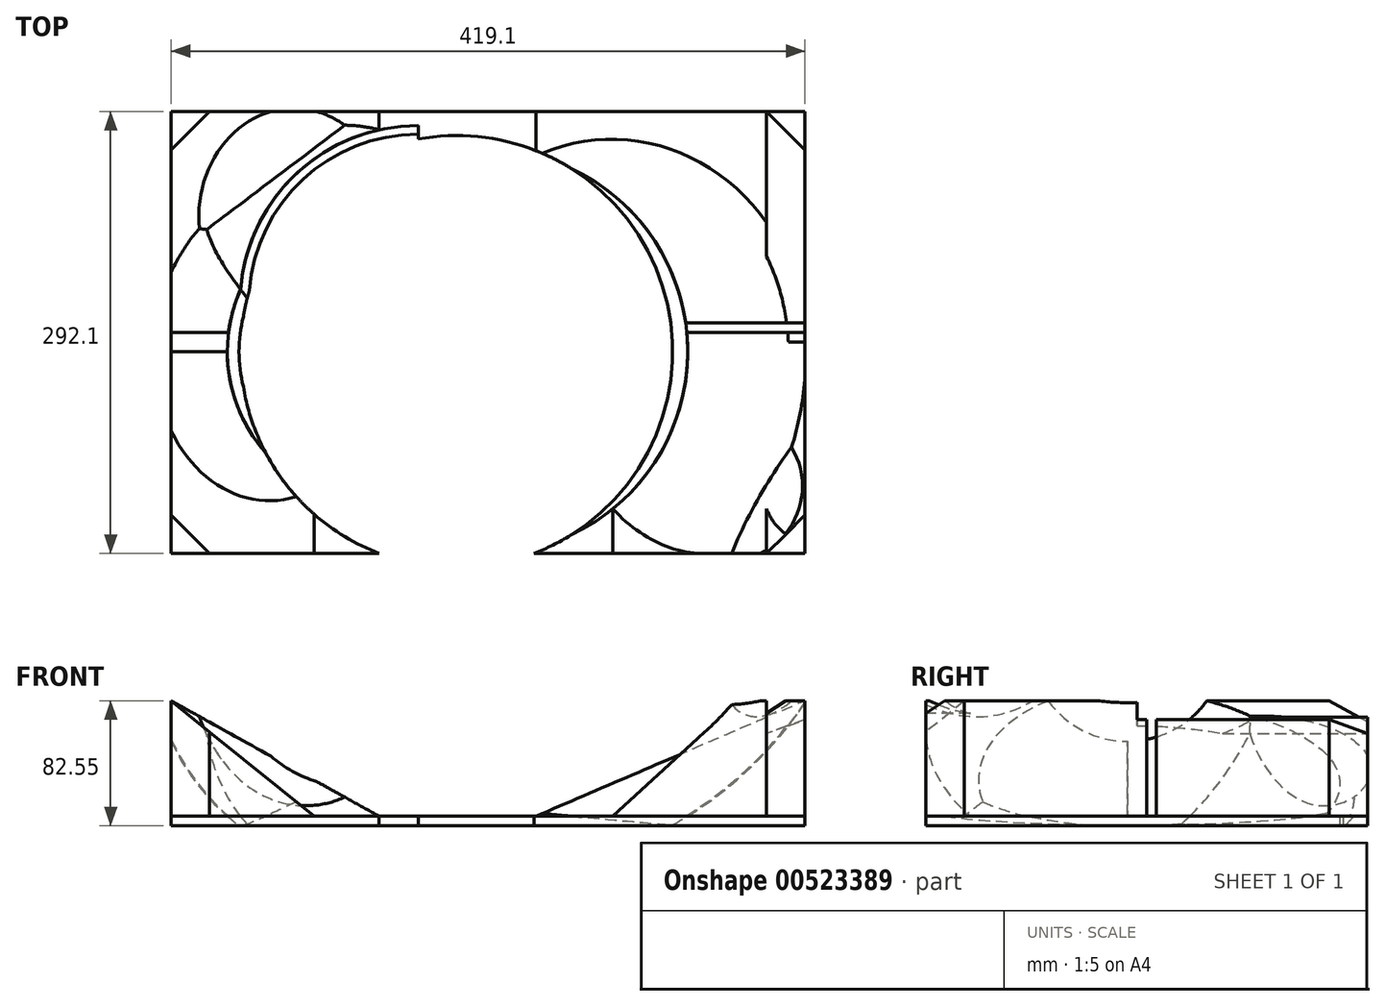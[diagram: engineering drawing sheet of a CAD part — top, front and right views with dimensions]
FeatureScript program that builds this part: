
annotation { "Feature Type Name" : "Feature", "Feature Type Description" : "" }
export const myFeature = defineFeature(function(context is Context, id is Id, definition is map)
    precondition{}
    {
        {
            var Q0;
            Q0=qCreatedBy(makeId("Top.planeOp"),FACE);
            var sketch = newSketch(context, id + "F0", { "sketchPlane" : qUnion([Q0])});
            skLineSegment(sketch, "E0.bottom", {"start": v(-188.72, 158.75) * mm, "end": v(230.38, 158.75) * mm});
            skLineSegment(sketch, "E0.top", {"start": v(-188.72, -133.35) * mm, "end": v(230.38, -133.35) * mm});
            skLineSegment(sketch, "E0.left", {"start": v(-188.72, 158.75) * mm, "end": v(-188.72, -133.35) * mm});
            skLineSegment(sketch, "E0.right", {"start": v(230.38, 158.75) * mm, "end": v(230.38, -133.35) * mm});
            skCircle(sketch, "E1", {"center": v(0, 0) * mm, "radius": 142.88 * mm});
            skSolve(sketch);
        }
        {
            var Q0;
            Q0=makeQuery(id+"F0.imprint","IMPRINT",FACE,{"disambiguationData":[TD([[makeQuery(id+"F0.imprint","IMPRINT",EDGE,{"derivedFrom":sQuery(id+"F0.wireOp",EDGE,"E0.bottom")}),-1.0]])]});
            extrude(context, id + "F1", {"entities" : qUnion([Q0]), "oppositeDirection" : true, "depth" : 6.35 * mm, "offsetDistance" : 25.4 * mm});
        }
        {
            var Q0;
            Q0=makeQuery(id+"F1.opExtrude","CAP_FACE",FACE,{"disambiguationData":[OSD([sQuery(id+"F0.wireOp",EDGE,"E0.bottom"),sQuery(id+"F0.wireOp",EDGE,"E0.top"),sQuery(id+"F0.wireOp",EDGE,"E0.left"),sQuery(id+"F0.wireOp",EDGE,"E0.right"),sQuery(id+"F0.wireOp",EDGE,"E1")])],"isStart":true});
            var sketch = newSketch(context, id + "F2", { "sketchPlane" : qUnion([Q0])});
            skLineSegment(sketch, "E2.bottom", {"start": v(230.38, 158.75) * mm, "end": v(52.58, 158.75) * mm});
            skLineSegment(sketch, "E2.top", {"start": v(230.38, 19.05) * mm, "end": v(52.58, 19.05) * mm});
            skLineSegment(sketch, "E2.left", {"start": v(230.38, 158.75) * mm, "end": v(230.38, 19.05) * mm});
            skLineSegment(sketch, "E2.right", {"start": v(52.58, 158.75) * mm, "end": v(52.58, 19.05) * mm});
            skLineSegment(sketch, "E3.bottom", {"start": v(230.38, -133.35) * mm, "end": v(103.38, -133.35) * mm});
            skLineSegment(sketch, "E3.top", {"start": v(230.38, 12.7) * mm, "end": v(103.38, 12.7) * mm});
            skLineSegment(sketch, "E3.left", {"start": v(230.38, -133.35) * mm, "end": v(230.38, 12.7) * mm});
            skLineSegment(sketch, "E3.right", {"start": v(103.38, -133.35) * mm, "end": v(103.38, 12.7) * mm});
            skLineSegment(sketch, "E4.bottom", {"start": v(-188.72, -133.35) * mm, "end": v(-94.22, -133.35) * mm});
            skLineSegment(sketch, "E4.top", {"start": v(-188.72, 0) * mm, "end": v(-94.22, 0) * mm});
            skLineSegment(sketch, "E4.left", {"start": v(-188.72, -133.35) * mm, "end": v(-188.72, 0) * mm});
            skLineSegment(sketch, "E4.right", {"start": v(-94.22, -133.35) * mm, "end": v(-94.22, 0) * mm});
            skLineSegment(sketch, "E5.bottom", {"start": v(-188.72, 158.75) * mm, "end": v(-51.3, 158.75) * mm});
            skLineSegment(sketch, "E5.top", {"start": v(-188.72, 12.7) * mm, "end": v(-51.3, 12.7) * mm});
            skLineSegment(sketch, "E5.left", {"start": v(-188.72, 158.75) * mm, "end": v(-188.72, 12.7) * mm});
            skLineSegment(sketch, "E5.right", {"start": v(-51.3, 158.75) * mm, "end": v(-51.3, 12.7) * mm});
            skSolve(sketch);
        }
        {
            var Q0;
            {var subQ1=sQuery(id+"F2.wireOp",EDGE,"E5.bottom");Q0=makeQuery(id+"F2.imprint","IMPRINT",FACE,{"disambiguationData":[TD([[makeQuery(id+"F2.imprint","IMPRINT",EDGE,{"derivedFrom":subQ1}),-1.0]])]});}
            var Q1;
            {var subQ1=sQuery(id+"F2.wireOp",EDGE,"E4.bottom");Q1=makeQuery(id+"F2.imprint","IMPRINT",FACE,{"disambiguationData":[TD([[makeQuery(id+"F2.imprint","IMPRINT",EDGE,{"derivedFrom":subQ1}),1.0]])]});}
            var Q2;
            {var subQ1=sQuery(id+"F2.wireOp",EDGE,"E3.bottom");Q2=makeQuery(id+"F2.imprint","IMPRINT",FACE,{"disambiguationData":[TD([[makeQuery(id+"F2.imprint","IMPRINT",EDGE,{"derivedFrom":subQ1}),1.0]])]});}
            var Q3;
            {var subQ1=sQuery(id+"F2.wireOp",EDGE,"E2.bottom");Q3=makeQuery(id+"F2.imprint","IMPRINT",FACE,{"disambiguationData":[TD([[makeQuery(id+"F2.imprint","IMPRINT",EDGE,{"derivedFrom":subQ1}),-1.0]])]});}
            extrude(context, id + "F3", {"entities" : qUnion([Q0, Q1, Q2, Q3]), "depth" : 76.2 * mm, "offsetDistance" : 25.4 * mm});
        }
        {
            var Q0;
            Q0=qCreatedBy(makeId("Front.planeOp"),FACE);
            var sketch = newSketch(context, id + "F4", { "sketchPlane" : qUnion([Q0])});
            skCircle(sketch, "E6", {"center": v(19.05, 215.9) * mm, "radius": 254 * mm});
            skLineSegment(sketch, "E7", {"start": v(0, -69.9) * mm, "end": v(0, 58.43) * mm, "construction": true});
            skLineSegment(sketch, "E8", {"start": v(19.05, 215.9) * mm, "end": v(19.05, 27.35) * mm, "construction": true});
            skLineSegment(sketch, "E9.bottom", {"start": v(-27.8, 483.75) * mm, "end": v(43, 483.75) * mm});
            skLineSegment(sketch, "E9.top", {"start": v(-27.8, -63.65) * mm, "end": v(43, -63.65) * mm});
            skLineSegment(sketch, "E9.left", {"start": v(-27.8, 483.75) * mm, "end": v(-27.8, -63.65) * mm});
            skLineSegment(sketch, "E9.right", {"start": v(43, 483.75) * mm, "end": v(43, -63.65) * mm});
            skSolve(sketch);
        }
        {
            var Q0;
            {var subQ0=sQuery(id+"F4.wireOp",EDGE,"E9.right");var subQ1=sQuery(id+"F4.wireOp",EDGE,"E6");var subQ2=makeQuery(id+"F4.imprint","INTERSECT",VERTEX,{"disambiguationData":[OD(0.0)],"derivedFrom":[subQ1,subQ0]});Q0=makeQuery(id+"F4.imprint","IMPRINT",FACE,{"disambiguationData":[TD([[makeQuery(id+"F4.imprint","IMPRINT",EDGE,{"disambiguationData":[TD([[subQ2,1.0]])],"derivedFrom":subQ1}),1.0]])]});}
            var Q1;
            Q1=sQuery(id+"F4.wireOp",EDGE,"E8");
            revolve(context, id + "F5", {"operationType" : NewBodyOperationType.REMOVE, "entities" : qUnion([Q0]), "axis" : qUnion([Q1]), "revolveType" : RevolveType.FULL, "oppositeDirection" : true});
        }
        {
            var Q0;
            Q0=qCreatedBy(makeId("Front.planeOp"),FACE);
            cPlane(context, id + "F6", {"entities" : qUnion([Q0]), "cplaneType" : CPlaneType.OFFSET, "offset" : 88.9 * mm, "width" : 152.4 * mm, "height" : 152.4 * mm});
        }
        {
            var Q0;
            Q0=qCreatedBy(makeId("Front.planeOp"),FACE);
            cPlane(context, id + "F7", {"entities" : qUnion([Q0]), "cplaneType" : CPlaneType.OFFSET, "offset" : 88.9 * mm, "oppositeDirection" : true, "width" : 152.4 * mm, "height" : 152.4 * mm});
        }
        {
            var Q0;
            Q0=qCreatedBy(id+"F6.planeOp",FACE);
            var sketch = newSketch(context, id + "F8", { "sketchPlane" : qUnion([Q0])});
            skCircle(sketch, "E10", {"center": v(179.58, 165.1) * mm, "radius": 101.6 * mm});
            skLineSegment(sketch, "E11", {"start": v(179.58, 165.1) * mm, "end": v(179.58, 73.44) * mm, "construction": true});
            skLineSegment(sketch, "E12", {"start": v(179.58, 105.87) * mm, "end": v(179.58, 266.7) * mm});
            skLineSegment(sketch, "E13", {"start": v(179.58, 179.8) * mm, "end": v(179.58, 63.5) * mm});
            skSolve(sketch);
        }
        {
            var Q0;
            {var subQ0=sQuery(id+"F8.wireOp",EDGE,"E12");var subQ1=sQuery(id+"F8.wireOp",EDGE,"E10");var subQ2=makeQuery(id+"F8.imprint","INTERSECT",VERTEX,{"disambiguationData":[OD(0.0)],"derivedFrom":[subQ1,subQ0]});Q0=makeQuery(id+"F8.imprint","IMPRINT",FACE,{"disambiguationData":[TD([[makeQuery(id+"F8.imprint","IMPRINT",EDGE,{"disambiguationData":[TD([[subQ2,1.0]])],"derivedFrom":subQ1}),1.0]])]});}
            var Q1;
            Q1=sQuery(id+"F8.wireOp",EDGE,"E12");
            revolve(context, id + "F9", {"operationType" : NewBodyOperationType.REMOVE, "entities" : qUnion([Q0]), "axis" : qUnion([Q1]), "revolveType" : RevolveType.FULL, "oppositeDirection" : true});
        }
        {
            var Q0;
            Q0=makeQuery(id+"F3.opExtrude","SWEPT_FACE",FACE,{"disambiguationData":[OSD([sQuery(id+"F2.wireOp",EDGE,"E3.bottom")])]});
            var sketch = newSketch(context, id + "F10", { "sketchPlane" : qUnion([Q0])});
            skLineSegment(sketch, "E14", {"start": v(103.38, 0) * mm, "end": v(170.86, 62) * mm});
            skLineSegment(sketch, "E15", {"start": v(170.86, 62) * mm, "end": v(86.04, 62) * mm});
            skLineSegment(sketch, "E16", {"start": v(86.04, 62) * mm, "end": v(86.04, 0) * mm});
            skLineSegment(sketch, "E17", {"start": v(86.04, 0) * mm, "end": v(103.38, 0) * mm});
            skSolve(sketch);
        }
        {
            var Q0;
            {var subQ0=sQuery(id+"F10.wireOp",EDGE,"E15");Q0=makeQuery(id+"F10.imprint","IMPRINT",FACE,{"disambiguationData":[TD([[makeQuery(id+"F10.imprint","IMPRINT",EDGE,{"derivedFrom":subQ0}),1.0]])]});}
            var Q1;
            {var subQ1=sQuery(id+"F2.wireOp",EDGE,"E3.bottom");var subQ2=makeQuery(id+"F3.opExtrude","SWEPT_EDGE",EDGE,{"disambiguationData":[OSD([sQuery(id+"F0.wireOp",EDGE,"E0.top"),subQ1,sQuery(id+"F2.wireOp",EDGE,"E3.right")])]});Q1=makeQuery(id+"F10.imprint","IMPRINT",FACE,{"disambiguationData":[TD([[makeQuery(id+"F10.imprint","IMPRINT",EDGE,{"derivedFrom":subQ2}),1.0]])]});}
            extrude(context, id + "F11", {"entities" : qUnion([Q0, Q1]), "operationType" : NewBodyOperationType.REMOVE, "oppositeDirection" : true, "depth" : 76.2 * mm, "offsetDistance" : 25.4 * mm});
        }
        {
            var Q0;
            Q0=makeQuery(id+"F3.opExtrude","CAP_FACE",FACE,{"disambiguationData":[OSD([sQuery(id+"F0.wireOp",EDGE,"E1"),sQuery(id+"F2.wireOp",EDGE,"E3.bottom"),sQuery(id+"F2.wireOp",EDGE,"E3.top"),sQuery(id+"F2.wireOp",EDGE,"E3.left"),sQuery(id+"F2.wireOp",EDGE,"E3.right")])],"isStart":true});
            var sketch = newSketch(context, id + "F12", { "sketchPlane" : qUnion([Q0])});
            skLineSegment(sketch, "E18.bottom", {"start": v(230.38, 133.35) * mm, "end": v(204.98, 133.35) * mm});
            skLineSegment(sketch, "E18.top", {"start": v(230.38, 107.95) * mm, "end": v(204.98, 107.95) * mm});
            skLineSegment(sketch, "E18.left", {"start": v(230.38, 133.35) * mm, "end": v(230.38, 107.95) * mm});
            skLineSegment(sketch, "E18.right", {"start": v(204.98, 133.35) * mm, "end": v(204.98, 107.95) * mm});
            skLineSegment(sketch, "E19", {"start": v(204.98, 133.35) * mm, "end": v(230.38, 107.95) * mm});
            skSolve(sketch);
        }
        {
            var Q0;
            Q0=makeQuery(id+"F12.imprint","IMPRINT",FACE,{"disambiguationData":[TD([[makeQuery(id+"F12.imprint","IMPRINT",EDGE,{"derivedFrom":sQuery(id+"F12.wireOp",EDGE,"E18.bottom")}),-1.0]])]});
            extrude(context, id + "F13", {"entities" : qUnion([Q0]), "operationType" : NewBodyOperationType.REMOVE, "oppositeDirection" : true, "depth" : 127 * mm, "offsetDistance" : 25.4 * mm});
        }
        {
            var Q0;
            Q0=makeQuery(id+"F3.opExtrude","SWEPT_FACE",FACE,{"disambiguationData":[OSD([sQuery(id+"F2.wireOp",EDGE,"E2.bottom")])]});
            var sketch = newSketch(context, id + "F14", { "sketchPlane" : qUnion([Q0])});
            skLineSegment(sketch, "E20", {"start": v(-52.58, 0) * mm, "end": v(-230.38, 76.2) * mm});
            skLineSegment(sketch, "E21", {"start": v(-230.38, 76.2) * mm, "end": v(-213, 128.04) * mm});
            skLineSegment(sketch, "E22", {"start": v(-213, 128.04) * mm, "end": v(-8.85, 51.85) * mm});
            skLineSegment(sketch, "E23", {"start": v(-8.85, 51.85) * mm, "end": v(-52.58, 0) * mm});
            skSolve(sketch);
        }
        {
            var Q0;
            Q0=makeQuery(id+"F14.imprint","IMPRINT",FACE,{"disambiguationData":[TD([[makeQuery(id+"F14.imprint","IMPRINT",EDGE,{"derivedFrom":sQuery(id+"F14.wireOp",EDGE,"E20")}),-1.0]])]});
            var Q1;
            Q1=makeQuery(id+"F14.imprint","IMPRINT",FACE,{"disambiguationData":[TD([[makeQuery(id+"F14.imprint","IMPRINT",EDGE,{"derivedFrom":sQuery(id+"F14.wireOp",EDGE,"E21")}),-1.0]])]});
            extrude(context, id + "F15", {"entities" : qUnion([Q0, Q1]), "operationType" : NewBodyOperationType.REMOVE, "oppositeDirection" : true, "depth" : 152.4 * mm, "offsetDistance" : 25.4 * mm});
        }
        {
            var Q0;
            Q0=makeQuery(id+"F3.opExtrude","SWEPT_FACE",FACE,{"disambiguationData":[OSD([sQuery(id+"F2.wireOp",EDGE,"E3.bottom")])]});
            var sketch = newSketch(context, id + "F16", { "sketchPlane" : qUnion([Q0])});
            skLineSegment(sketch, "E24", {"start": v(103.38, 0) * mm, "end": v(231.36, 85.5) * mm});
            skLineSegment(sketch, "E25", {"start": v(231.36, 85.5) * mm, "end": v(81.68, 94.74) * mm});
            skLineSegment(sketch, "E26", {"start": v(81.68, 94.74) * mm, "end": v(103.38, 0) * mm});
            skSolve(sketch);
        }
        {
            var Q0;
            {var subQ3=sQuery(id+"F16.wireOp",EDGE,"E25");Q0=makeQuery(id+"F16.imprint","IMPRINT",FACE,{"disambiguationData":[TD([[makeQuery(id+"F16.imprint","IMPRINT",EDGE,{"derivedFrom":subQ3}),1.0]])]});}
            var Q1;
            {var subQ10=sQuery(id+"F10.wireOp",EDGE,"E14");var subQ11=makeQuery(id+"F11.boolean.opBoolean","COPY",EDGE,{"derivedFrom":makeQuery(id+"F11.opExtrude","CAP_EDGE",EDGE,{"disambiguationData":[OSD([subQ10])],"isStart":true})});Q1=makeQuery(id+"F16.imprint","IMPRINT",FACE,{"disambiguationData":[TD([[makeQuery(id+"F16.imprint","IMPRINT",EDGE,{"derivedFrom":subQ11}),-1.0]])]});}
            extrude(context, id + "F17", {"entities" : qUnion([Q0, Q1]), "operationType" : NewBodyOperationType.REMOVE, "oppositeDirection" : true, "depth" : 152.4 * mm, "offsetDistance" : 25.4 * mm});
        }
        {
            var Q0;
            Q0=makeQuery(id+"F3.opExtrude","CAP_FACE",FACE,{"disambiguationData":[OSD([sQuery(id+"F0.wireOp",EDGE,"E1"),sQuery(id+"F2.wireOp",EDGE,"E2.bottom"),sQuery(id+"F2.wireOp",EDGE,"E2.top"),sQuery(id+"F2.wireOp",EDGE,"E2.left"),sQuery(id+"F2.wireOp",EDGE,"E2.right")])],"isStart":true});
            var sketch = newSketch(context, id + "F18", { "sketchPlane" : qUnion([Q0])});
            skLineSegment(sketch, "E27.bottom", {"start": v(230.38, -158.75) * mm, "end": v(204.98, -158.75) * mm});
            skLineSegment(sketch, "E27.top", {"start": v(230.38, -133.35) * mm, "end": v(204.98, -133.35) * mm});
            skLineSegment(sketch, "E27.left", {"start": v(230.38, -158.75) * mm, "end": v(230.38, -133.35) * mm});
            skLineSegment(sketch, "E27.right", {"start": v(204.98, -158.75) * mm, "end": v(204.98, -133.35) * mm});
            skLineSegment(sketch, "E28", {"start": v(230.38, -133.35) * mm, "end": v(204.98, -158.75) * mm});
            skSolve(sketch);
        }
        {
            var Q0;
            Q0=makeQuery(id+"F18.imprint","IMPRINT",FACE,{"disambiguationData":[TD([[makeQuery(id+"F18.imprint","IMPRINT",EDGE,{"derivedFrom":sQuery(id+"F18.wireOp",EDGE,"E27.bottom")}),1.0]])]});
            var Q1;
            Q1=makeQuery(id+"F15.boolean.opBoolean","COPY",FACE,{"derivedFrom":makeQuery(id+"F15.opExtrude","SWEPT_FACE",FACE,{"disambiguationData":[OSD([sQuery(id+"F14.wireOp",EDGE,"E20")])]})});
            extrude(context, id + "F19", {"entities" : qUnion([Q0]), "operationType" : NewBodyOperationType.REMOVE, "endBound" : BoundingType.UP_TO_SURFACE, "oppositeDirection" : true, "depth" : 25.4 * mm, "endBoundEntityFace" : qUnion([Q1]), "offsetDistance" : 25.4 * mm});
        }
        {
            var Q0;
            Q0=makeQuery(id+"F3.opExtrude","SWEPT_FACE",FACE,{"disambiguationData":[OSD([sQuery(id+"F2.wireOp",EDGE,"E2.bottom")])]});
            var sketch = newSketch(context, id + "F20", { "sketchPlane" : qUnion([Q0])});
            skLineSegment(sketch, "E29", {"start": v(-52.58, 0) * mm, "end": v(-247.38, 69.92) * mm});
            skLineSegment(sketch, "E30", {"start": v(-247.38, 69.92) * mm, "end": v(-247.38, 121) * mm});
            skLineSegment(sketch, "E31", {"start": v(-247.38, 121) * mm, "end": v(-166.02, 113.82) * mm});
            skLineSegment(sketch, "E32", {"start": v(-166.02, 113.82) * mm, "end": v(-52.58, 0) * mm});
            skSolve(sketch);
        }
        {
            var Q0;
            {var subQ0=sQuery(id+"F20.wireOp",EDGE,"E30");Q0=makeQuery(id+"F20.imprint","IMPRINT",FACE,{"disambiguationData":[TD([[makeQuery(id+"F20.imprint","IMPRINT",EDGE,{"derivedFrom":subQ0}),-1.0]])]});}
            var Q1;
            {var subQ1=makeQuery(id+"F15.boolean.opBoolean","COPY",EDGE,{"derivedFrom":makeQuery(id+"F15.opExtrude","CAP_EDGE",EDGE,{"disambiguationData":[OSD([sQuery(id+"F14.wireOp",EDGE,"E20")])],"isStart":true})});Q1=makeQuery(id+"F20.imprint","IMPRINT",FACE,{"disambiguationData":[TD([[makeQuery(id+"F20.imprint","IMPRINT",EDGE,{"derivedFrom":subQ1}),1.0]])]});}
            extrude(context, id + "F21", {"entities" : qUnion([Q0, Q1]), "operationType" : NewBodyOperationType.REMOVE, "oppositeDirection" : true, "depth" : 152.4 * mm, "offsetDistance" : 25.4 * mm});
        }
        {
            var Q0;
            Q0=qCreatedBy(makeId("Front.planeOp"),FACE);
            var sketch = newSketch(context, id + "F22", { "sketchPlane" : qUnion([Q0])});
            skCircle(sketch, "E33", {"center": v(-50.8, 114.3) * mm, "radius": 152.4 * mm});
            skLineSegment(sketch, "E34", {"start": v(-50.8, 114.3) * mm, "end": v(-50.8, -19.04) * mm, "construction": true});
            skLineSegment(sketch, "E35", {"start": v(-50.8, 13.4) * mm, "end": v(-50.8, 266.7) * mm});
            skLineSegment(sketch, "E36", {"start": v(-50.8, 87.32) * mm, "end": v(-50.8, -38.1) * mm});
            skSolve(sketch);
        }
        {
            var Q0;
            {var subQ0=sQuery(id+"F22.wireOp",EDGE,"E35");Q0=makeQuery(id+"F22.imprint","IMPRINT",FACE,{"disambiguationData":[TD([[makeQuery(id+"F22.imprint","IMPRINT",EDGE,{"derivedFrom":subQ0}),1.0]])]});}
            var Q1;
            Q1=sQuery(id+"F22.wireOp",EDGE,"E35");
            revolve(context, id + "F23", {"operationType" : NewBodyOperationType.REMOVE, "entities" : qUnion([Q0]), "axis" : qUnion([Q1]), "revolveType" : RevolveType.FULL, "oppositeDirection" : true});
        }
        {
            var Q0;
            Q0=makeQuery(id+"F3.opExtrude","SWEPT_FACE",FACE,{"disambiguationData":[OSD([sQuery(id+"F2.wireOp",EDGE,"E4.bottom")])]});
            var sketch = newSketch(context, id + "F24", { "sketchPlane" : qUnion([Q0])});
            skLineSegment(sketch, "E37", {"start": v(-94.22, 0) * mm, "end": v(-188.72, 76.2) * mm});
            skLineSegment(sketch, "E38", {"start": v(-188.72, 76.2) * mm, "end": v(-166.85, 100.39) * mm});
            skLineSegment(sketch, "E39", {"start": v(-166.85, 100.39) * mm, "end": v(-77, 100.39) * mm});
            skLineSegment(sketch, "E40", {"start": v(-77, 100.39) * mm, "end": v(-40.79, 17.2) * mm});
            skLineSegment(sketch, "E41", {"start": v(-40.79, 17.2) * mm, "end": v(-94.22, 0) * mm});
            skSolve(sketch);
        }
        {
            var Q0;
            Q0=makeQuery(id+"F24.imprint","IMPRINT",FACE,{"disambiguationData":[TD([[makeQuery(id+"F24.imprint","IMPRINT",EDGE,{"derivedFrom":sQuery(id+"F24.wireOp",EDGE,"E38")}),-1.0]])]});
            var Q1;
            Q1=makeQuery(id+"F24.imprint","IMPRINT",FACE,{"disambiguationData":[TD([[makeQuery(id+"F24.imprint","IMPRINT",EDGE,{"derivedFrom":sQuery(id+"F24.wireOp",EDGE,"E37")}),-1.0]])]});
            extrude(context, id + "F25", {"entities" : qUnion([Q0, Q1]), "operationType" : NewBodyOperationType.REMOVE, "oppositeDirection" : true, "depth" : 152.4 * mm, "offsetDistance" : 25.4 * mm});
        }
        {
            var Q0;
            Q0=makeQuery(id+"F3.opExtrude","SWEPT_FACE",FACE,{"disambiguationData":[OSD([sQuery(id+"F2.wireOp",EDGE,"E5.bottom")])]});
            var sketch = newSketch(context, id + "F26", { "sketchPlane" : qUnion([Q0])});
            skLineSegment(sketch, "E42", {"start": v(51.3, 0) * mm, "end": v(188.72, 76.2) * mm});
            skLineSegment(sketch, "E43", {"start": v(188.72, 76.2) * mm, "end": v(202.68, 107.68) * mm});
            skLineSegment(sketch, "E44", {"start": v(202.68, 107.68) * mm, "end": v(16.03, 114.1) * mm});
            skLineSegment(sketch, "E45", {"start": v(16.03, 114.1) * mm, "end": v(51.3, 0) * mm});
            skSolve(sketch);
        }
        {
            var Q0;
            Q0=makeQuery(id+"F26.imprint","IMPRINT",FACE,{"disambiguationData":[TD([[makeQuery(id+"F26.imprint","IMPRINT",EDGE,{"derivedFrom":sQuery(id+"F26.wireOp",EDGE,"E42")}),1.0]])]});
            var Q1;
            Q1=makeQuery(id+"F26.imprint","IMPRINT",FACE,{"disambiguationData":[TD([[makeQuery(id+"F26.imprint","IMPRINT",EDGE,{"derivedFrom":sQuery(id+"F26.wireOp",EDGE,"E43")}),1.0]])]});
            extrude(context, id + "F27", {"entities" : qUnion([Q0, Q1]), "operationType" : NewBodyOperationType.REMOVE, "oppositeDirection" : true, "depth" : 152.4 * mm, "offsetDistance" : 25.4 * mm});
        }
        {
            var Q0;
            Q0=qCreatedBy(id+"F7.planeOp",FACE);
            var sketch = newSketch(context, id + "F28", { "sketchPlane" : qUnion([Q0])});
            skCircle(sketch, "E46", {"center": v(-68.58, 101.6) * mm, "radius": 107.95 * mm});
            skLineSegment(sketch, "E47", {"start": v(-68.58, -6.35) * mm, "end": v(-68.58, 209.55) * mm});
            skSolve(sketch);
        }
        {
            var Q0;
            {var subQ0=sQuery(id+"F28.wireOp",EDGE,"E47");Q0=makeQuery(id+"F28.imprint","IMPRINT",FACE,{"disambiguationData":[TD([[makeQuery(id+"F28.imprint","IMPRINT",EDGE,{"derivedFrom":subQ0}),1.0]])]});}
            var Q1;
            Q1=sQuery(id+"F28.wireOp",EDGE,"E47");
            revolve(context, id + "F29", {"operationType" : NewBodyOperationType.REMOVE, "entities" : qUnion([Q0]), "axis" : qUnion([Q1]), "revolveType" : RevolveType.FULL, "oppositeDirection" : true});
        }
        {
            var Q0;
            Q0=makeQuery(id+"F3.opExtrude","CAP_FACE",FACE,{"disambiguationData":[OSD([sQuery(id+"F0.wireOp",EDGE,"E1"),sQuery(id+"F2.wireOp",EDGE,"E4.bottom"),sQuery(id+"F2.wireOp",EDGE,"E4.top"),sQuery(id+"F2.wireOp",EDGE,"E4.left"),sQuery(id+"F2.wireOp",EDGE,"E4.right")])],"isStart":true});
            var sketch = newSketch(context, id + "F30", { "sketchPlane" : qUnion([Q0])});
            skLineSegment(sketch, "E48.bottom", {"start": v(-188.72, 133.35) * mm, "end": v(-163.32, 133.35) * mm});
            skLineSegment(sketch, "E48.top", {"start": v(-188.72, 107.95) * mm, "end": v(-163.32, 107.95) * mm});
            skLineSegment(sketch, "E48.left", {"start": v(-188.72, 133.35) * mm, "end": v(-188.72, 107.95) * mm});
            skLineSegment(sketch, "E48.right", {"start": v(-163.32, 133.35) * mm, "end": v(-163.32, 107.95) * mm});
            skLineSegment(sketch, "E49", {"start": v(-188.72, 107.95) * mm, "end": v(-163.32, 133.35) * mm});
            skSolve(sketch);
        }
        {
            var Q0;
            Q0=makeQuery(id+"F30.imprint","IMPRINT",FACE,{"disambiguationData":[TD([[makeQuery(id+"F30.imprint","IMPRINT",EDGE,{"derivedFrom":sQuery(id+"F30.wireOp",EDGE,"E48.bottom")}),-1.0]])]});
            extrude(context, id + "F31", {"entities" : qUnion([Q0]), "operationType" : NewBodyOperationType.REMOVE, "endBound" : BoundingType.UP_TO_NEXT, "oppositeDirection" : true, "depth" : 25.4 * mm, "offsetDistance" : 25.4 * mm});
        }
        {
            var Q0;
            Q0=makeQuery(id+"F3.opExtrude","CAP_FACE",FACE,{"disambiguationData":[OSD([sQuery(id+"F0.wireOp",EDGE,"E1"),sQuery(id+"F2.wireOp",EDGE,"E5.bottom"),sQuery(id+"F2.wireOp",EDGE,"E5.top"),sQuery(id+"F2.wireOp",EDGE,"E5.left"),sQuery(id+"F2.wireOp",EDGE,"E5.right")])],"isStart":true});
            var sketch = newSketch(context, id + "F32", { "sketchPlane" : qUnion([Q0])});
            skLineSegment(sketch, "E50.bottom", {"start": v(-188.72, -158.75) * mm, "end": v(-163.32, -158.75) * mm});
            skLineSegment(sketch, "E50.top", {"start": v(-188.72, -133.35) * mm, "end": v(-163.32, -133.35) * mm});
            skLineSegment(sketch, "E50.left", {"start": v(-188.72, -158.75) * mm, "end": v(-188.72, -133.35) * mm});
            skLineSegment(sketch, "E50.right", {"start": v(-163.32, -158.75) * mm, "end": v(-163.32, -133.35) * mm});
            skLineSegment(sketch, "E51", {"start": v(-188.72, -133.35) * mm, "end": v(-163.32, -158.75) * mm});
            skSolve(sketch);
        }
        {
            var Q0;
            Q0=makeQuery(id+"F32.imprint","IMPRINT",FACE,{"disambiguationData":[TD([[makeQuery(id+"F32.imprint","IMPRINT",EDGE,{"derivedFrom":sQuery(id+"F32.wireOp",EDGE,"E50.bottom")}),1.0]])]});
            extrude(context, id + "F33", {"entities" : qUnion([Q0]), "operationType" : NewBodyOperationType.REMOVE, "endBound" : BoundingType.UP_TO_NEXT, "oppositeDirection" : true, "depth" : 25.4 * mm, "offsetDistance" : 25.4 * mm});
        }
        {
            var Q0;
            Q0=qCreatedBy(makeId("Front.planeOp"),FACE);
            cPlane(context, id + "F34", {"entities" : qUnion([Q0]), "cplaneType" : CPlaneType.OFFSET, "offset" : 31.75 * mm, "oppositeDirection" : true, "width" : 152.4 * mm, "height" : 152.4 * mm});
        }
        {
            var Q0;
            Q0=qCreatedBy(id+"F34.planeOp",FACE);
            var sketch = newSketch(context, id + "F35", { "sketchPlane" : qUnion([Q0])});
            skCircle(sketch, "E52", {"center": v(-25.4, 101.6) * mm, "radius": 155.58 * mm});
            skLineSegment(sketch, "E53", {"start": v(-25.4, -53.98) * mm, "end": v(-25.4, 257.18) * mm});
            skSolve(sketch);
        }
        {
            var Q0;
            {var subQ0=sQuery(id+"F35.wireOp",EDGE,"E53");Q0=makeQuery(id+"F35.imprint","IMPRINT",FACE,{"disambiguationData":[TD([[makeQuery(id+"F35.imprint","IMPRINT",EDGE,{"derivedFrom":subQ0}),1.0]])]});}
            var Q1;
            Q1=sQuery(id+"F35.wireOp",EDGE,"E53");
            revolve(context, id + "F36", {"operationType" : NewBodyOperationType.REMOVE, "entities" : qUnion([Q0]), "axis" : qUnion([Q1]), "revolveType" : RevolveType.SYMMETRIC, "oppositeDirection" : true, "angle" : 180 * degree});
        }
    });
